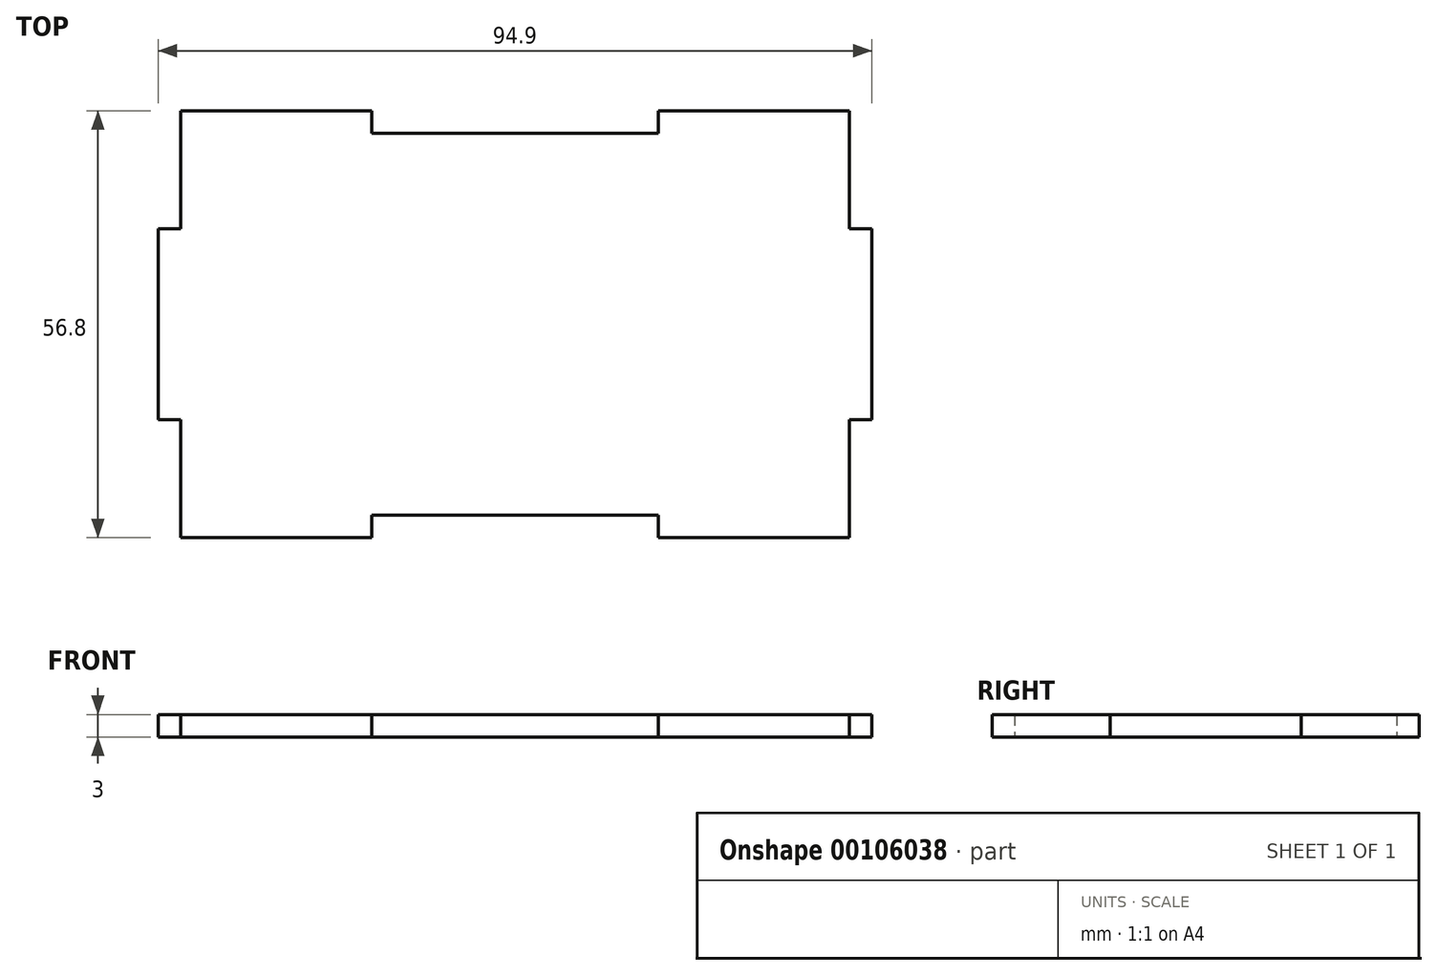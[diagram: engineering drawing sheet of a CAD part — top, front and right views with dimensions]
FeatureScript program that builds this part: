
annotation { "Feature Type Name" : "Feature", "Feature Type Description" : "" }
export const myFeature = defineFeature(function(context is Context, id is Id, definition is map)
    precondition{}
    {
        {
            var Q0;
            Q0=qCreatedBy(makeId("Top.planeOp"),FACE);
            var sketch = newSketch(context, id + "F0", { "sketchPlane" : qUnion([Q0])});
            skLineSegment(sketch, "E0", {"start": v(0, 0) * mm, "end": v(19.05, 0) * mm});
            skLineSegment(sketch, "E1", {"start": v(19.05, 0) * mm, "end": v(19.05, 3) * mm});
            skLineSegment(sketch, "E2", {"start": v(19.05, 3) * mm, "end": v(44.45, 3) * mm});
            skLineSegment(sketch, "E3", {"start": v(44.45, 3) * mm, "end": v(44.45, 0) * mm});
            skLineSegment(sketch, "E4", {"start": v(44.45, -12.7) * mm, "end": v(47.45, -12.7) * mm});
            skLineSegment(sketch, "E5", {"start": v(47.45, -12.7) * mm, "end": v(47.45, -25.4) * mm});
            skLineSegment(sketch, "E6.MirrorCS", {"start": v(-19.05, 0) * mm, "end": v(-19.05, 3) * mm});
            skLineSegment(sketch, "E7.MirrorCS", {"start": v(-47.45, -12.7) * mm, "end": v(-47.45, -25.4) * mm});
            skLineSegment(sketch, "E8.MirrorCS", {"start": v(0, 0) * mm, "end": v(-19.05, 0) * mm});
            skLineSegment(sketch, "E9.MirrorCS", {"start": v(-44.45, -12.7) * mm, "end": v(-47.45, -12.7) * mm});
            skLineSegment(sketch, "E10.MirrorCS", {"start": v(-19.05, 3) * mm, "end": v(-44.45, 3) * mm});
            skLineSegment(sketch, "E11.MirrorCS", {"start": v(-44.45, 3) * mm, "end": v(-44.45, 0) * mm});
            skLineSegment(sketch, "E12", {"start": v(-47.45, -25.4) * mm, "end": v(47.45, -25.4) * mm, "construction": true});
            skLineSegment(sketch, "E13.MirrorCS", {"start": v(-44.45, -53.8) * mm, "end": v(-44.45, -50.8) * mm});
            skLineSegment(sketch, "E14.MirrorCS", {"start": v(19.05, -50.8) * mm, "end": v(19.05, -53.8) * mm});
            skLineSegment(sketch, "E15.MirrorCS", {"start": v(44.45, -53.8) * mm, "end": v(44.45, -50.8) * mm});
            skLineSegment(sketch, "E16.MirrorCS", {"start": v(-19.05, -50.8) * mm, "end": v(-19.05, -53.8) * mm});
            skLineSegment(sketch, "E17.MirrorCS", {"start": v(47.45, -38.1) * mm, "end": v(47.45, -25.4) * mm});
            skLineSegment(sketch, "E18.MirrorCS", {"start": v(-19.05, -53.8) * mm, "end": v(-44.45, -53.8) * mm});
            skLineSegment(sketch, "E19.MirrorCS", {"start": v(-44.45, -38.1) * mm, "end": v(-47.45, -38.1) * mm});
            skLineSegment(sketch, "E20.MirrorCS", {"start": v(0, -50.8) * mm, "end": v(19.05, -50.8) * mm});
            skLineSegment(sketch, "E21.MirrorCS", {"start": v(19.05, -53.8) * mm, "end": v(44.45, -53.8) * mm});
            skLineSegment(sketch, "E22.MirrorCS", {"start": v(44.45, -38.1) * mm, "end": v(47.45, -38.1) * mm});
            skLineSegment(sketch, "E23.MirrorCS", {"start": v(-47.45, -38.1) * mm, "end": v(-47.45, -25.4) * mm});
            skLineSegment(sketch, "E24.MirrorCS", {"start": v(0, -50.8) * mm, "end": v(-19.05, -50.8) * mm});
            skLineSegment(sketch, "E25", {"start": v(-44.45, 0) * mm, "end": v(-44.45, -12.7) * mm});
            skLineSegment(sketch, "E26", {"start": v(-44.45, -38.1) * mm, "end": v(-44.45, -50.8) * mm});
            skLineSegment(sketch, "E27", {"start": v(44.45, 0) * mm, "end": v(44.45, -12.7) * mm});
            skLineSegment(sketch, "E28", {"start": v(44.45, -38.1) * mm, "end": v(44.45, -50.8) * mm});
            skSolve(sketch);
        }
        {
            var Q0;
            Q0=makeQuery(id+"F0.imprint","IMPRINT",FACE,{"disambiguationData":[TD([[makeQuery(id+"F0.imprint","IMPRINT",EDGE,{"derivedFrom":sQuery(id+"F0.wireOp",EDGE,"E3")}),-1.0]])]});
            extrude(context, id + "F1", {"entities" : qUnion([Q0]), "depth" : 3 * mm});
        }
    });
